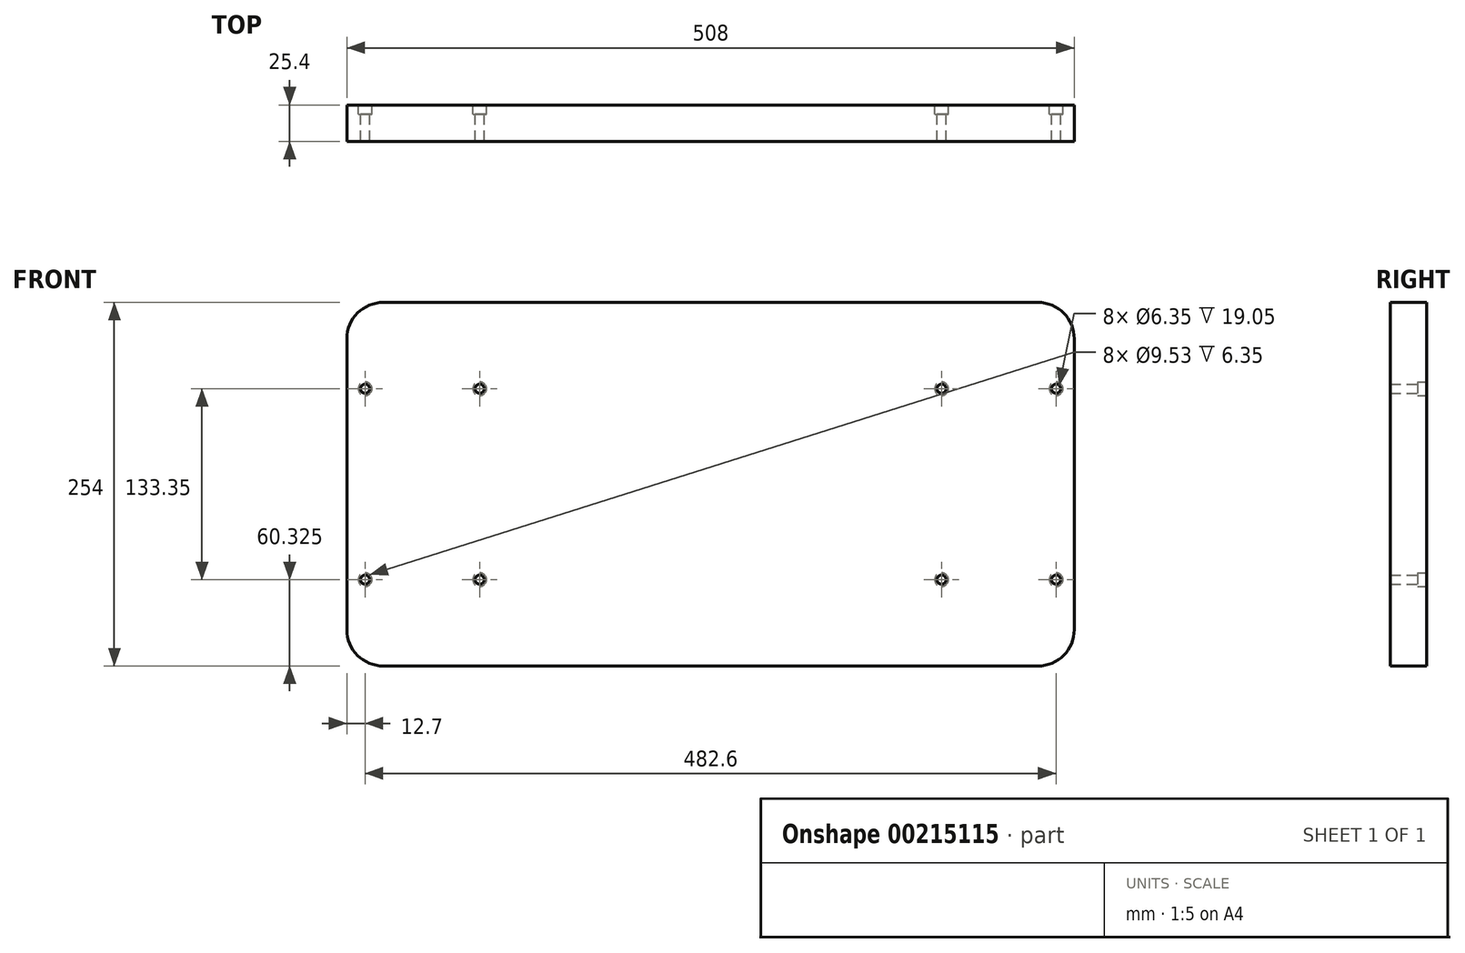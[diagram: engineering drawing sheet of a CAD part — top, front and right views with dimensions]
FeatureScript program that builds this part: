
annotation { "Feature Type Name" : "Feature", "Feature Type Description" : "" }
export const myFeature = defineFeature(function(context is Context, id is Id, definition is map)
    precondition{}
    {
        {
            var Q0;
            Q0=qCreatedBy(makeId("Front.planeOp"),FACE);
            var sketch = newSketch(context, id + "F0", { "sketchPlane" : qUnion([Q0])});
            skLineSegment(sketch, "E0", {"start": v(0, 25.4) * mm, "end": v(0, 228.6) * mm});
            skLineSegment(sketch, "E1", {"start": v(25.4, 254) * mm, "end": v(482.6, 254) * mm});
            skLineSegment(sketch, "E2", {"start": v(508, 228.6) * mm, "end": v(508, 25.4) * mm});
            skLineSegment(sketch, "E3", {"start": v(25.4, 0) * mm, "end": v(482.6, 0) * mm});
            skArc(sketch, "E4", {"start": v(0, 25.4) * mm, "mid": v(7.44, 7.44) * mm, "end": v(25.4, 0) * mm});
            skArc(sketch, "E5", {"start": v(25.4, 254) * mm, "mid": v(7.44, 246.56) * mm, "end": v(0, 228.6) * mm});
            skArc(sketch, "E6", {"start": v(508, 228.6) * mm, "mid": v(500.56, 246.56) * mm, "end": v(482.6, 254) * mm});
            skArc(sketch, "E7", {"start": v(482.6, 0) * mm, "mid": v(500.56, 7.44) * mm, "end": v(508, 25.4) * mm});
            skLineSegment(sketch, "E8", {"start": v(254, 254) * mm, "end": v(254, 0) * mm, "construction": true});
            skLineSegment(sketch, "E9", {"start": v(0, 127) * mm, "end": v(508, 127) * mm, "construction": true});
            skLineSegment(sketch, "E10", {"start": v(69.71, 127) * mm, "end": v(69.71, 193.67) * mm, "construction": true});
            skLineSegment(sketch, "E11", {"start": v(0, 193.67) * mm, "end": v(12.7, 193.67) * mm, "construction": true});
            skLineSegment(sketch, "E12", {"start": v(12.7, 193.67) * mm, "end": v(92.71, 193.67) * mm});
            skLineSegment(sketch, "E13.MirrorCS", {"start": v(12.7, 60.32) * mm, "end": v(92.71, 60.32) * mm});
            skLineSegment(sketch, "E14.MirrorCS", {"start": v(0, 60.32) * mm, "end": v(12.7, 60.32) * mm, "construction": true});
            skLineSegment(sketch, "E15.MirrorCS", {"start": v(69.71, 127) * mm, "end": v(69.71, 60.32) * mm, "construction": true});
            skLineSegment(sketch, "E16.MirrorCS", {"start": v(508, 193.67) * mm, "end": v(495.3, 193.67) * mm, "construction": true});
            skLineSegment(sketch, "E17.MirrorCS", {"start": v(495.3, 193.67) * mm, "end": v(415.3, 193.67) * mm});
            skLineSegment(sketch, "E18.MirrorCS", {"start": v(438.29, 127) * mm, "end": v(438.29, 193.67) * mm, "construction": true});
            skLineSegment(sketch, "E19.MirrorCS", {"start": v(438.29, 127) * mm, "end": v(438.29, 60.32) * mm, "construction": true});
            skLineSegment(sketch, "E20.MirrorCS", {"start": v(495.3, 60.32) * mm, "end": v(415.3, 60.32) * mm});
            skLineSegment(sketch, "E21.MirrorCS", {"start": v(508, 60.32) * mm, "end": v(495.3, 60.32) * mm, "construction": true});
            skSolve(sketch);
        }
        {
            var Q0;
            Q0 = qSketchRegion(id + "F0", true);
            extrude(context, id + "F1", {"entities" : qUnion([Q0]), "depth" : 25.4 * mm});
        }
        {
            var Q0;
            Q0=sQuery(id+"F0.wireOp",VERTEX,"E11.end");
            var Q1;
            Q1=sQuery(id+"F0.wireOp",VERTEX,"E12.end");
            var Q2;
            Q2=sQuery(id+"F0.wireOp",VERTEX,"E14.MirrorCS.end");
            var Q3;
            Q3=sQuery(id+"F0.wireOp",VERTEX,"E13.MirrorCS.end");
            var Q4;
            Q4=sQuery(id+"F0.wireOp",VERTEX,"E17.MirrorCS.end");
            var Q5;
            Q5=sQuery(id+"F0.wireOp",VERTEX,"E17.MirrorCS.start");
            var Q6;
            Q6=sQuery(id+"F0.wireOp",VERTEX,"E20.MirrorCS.end");
            var Q7;
            Q7=sQuery(id+"F0.wireOp",VERTEX,"E21.MirrorCS.end");
            var Q8;
            Q8=makeQuery(id+"F1.opExtrude","SWEPT_BODY",BODY,{"disambiguationData":[OSD([sQuery(id+"F0.wireOp",EDGE,"E0"),sQuery(id+"F0.wireOp",EDGE,"E1"),sQuery(id+"F0.wireOp",EDGE,"E2"),sQuery(id+"F0.wireOp",EDGE,"E3"),sQuery(id+"F0.wireOp",EDGE,"E4"),sQuery(id+"F0.wireOp",EDGE,"E5"),sQuery(id+"F0.wireOp",EDGE,"E6"),sQuery(id+"F0.wireOp",EDGE,"E7")])]});
            hole(context, id + "F2", {"style" : HoleStyle.C_BORE, "endStyle" : HoleEndStyle.THROUGH, "oppositeDirection" : true, "holeDiameter" : 6.35 * mm, "cBoreDiameter" : 9.52 * mm, "cBoreDepth" : 6.35 * mm, "locations" : qUnion([Q0, Q1, Q2, Q3, Q4, Q5, Q6, Q7]), "scope" : qUnion([Q8]), "isTappedThrough" : true});
        }
    });
